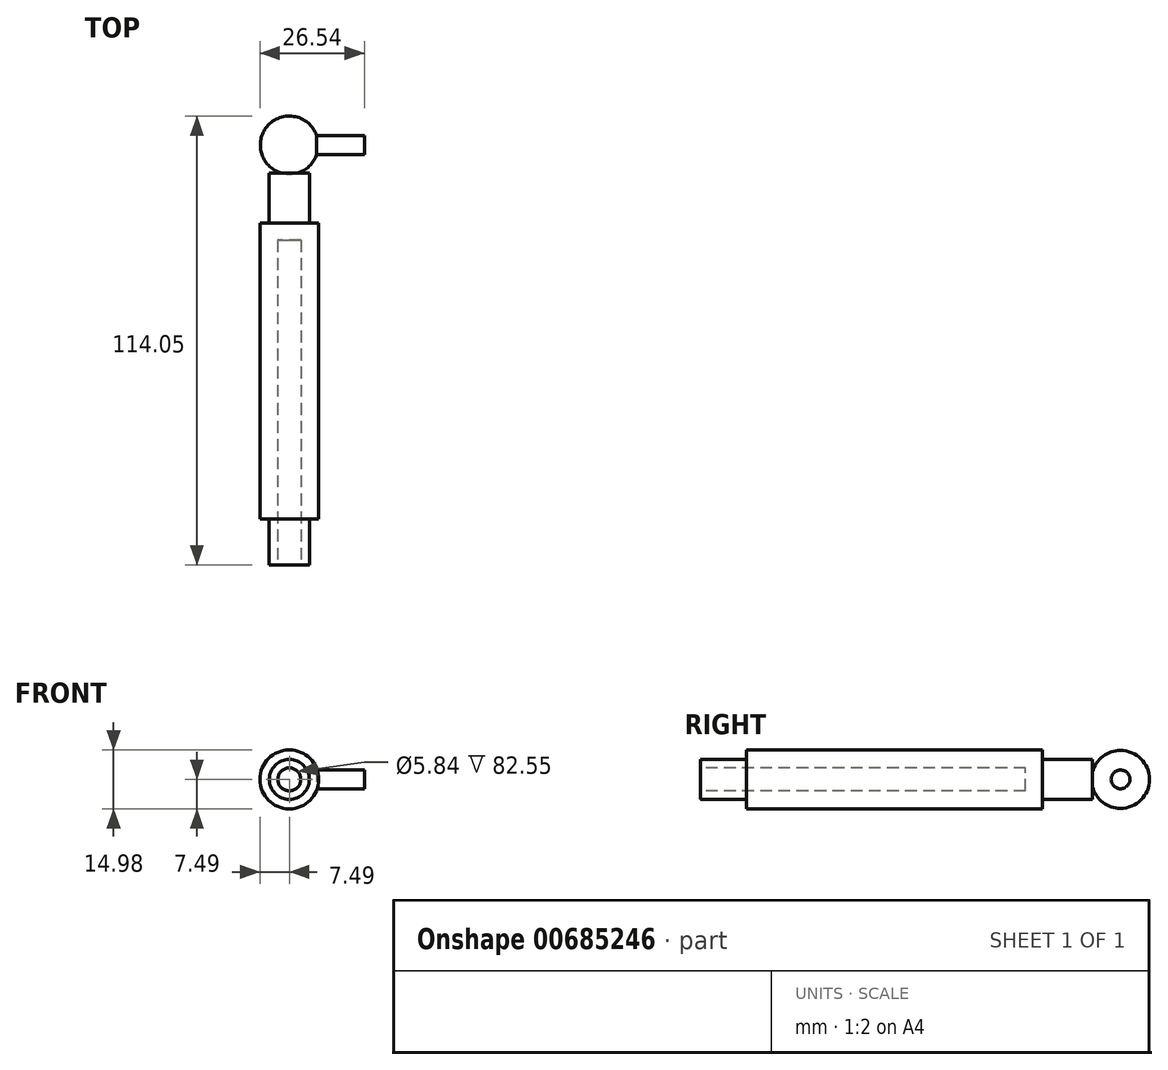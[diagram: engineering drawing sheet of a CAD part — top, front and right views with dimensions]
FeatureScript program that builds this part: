
annotation { "Feature Type Name" : "Feature", "Feature Type Description" : "" }
export const myFeature = defineFeature(function(context is Context, id is Id, definition is map)
    precondition{}
    {
        {
            var Q0;
            Q0=qCreatedBy(makeId("Front.planeOp"),FACE);
            var sketch = newSketch(context, id + "F0", { "sketchPlane" : qUnion([Q0])});
            skCircle(sketch, "E0", {"center": v(0, 0) * mm, "radius": 7.5 * mm});
            skSolve(sketch);
        }
        {
            var Q0;
            Q0 = qSketchRegion(id + "F0", true);
            extrude(context, id + "F1", {"entities" : qUnion([Q0]), "depth" : 75.18 * mm, "offsetDistance" : 25.4 * mm});
        }
        {
            var Q0;
            Q0=makeQuery(id+"F1.opExtrude","CAP_FACE",FACE,{"disambiguationData":[OSD([sQuery(id+"F0.wireOp",EDGE,"E0")])],"isStart":true});
            var sketch = newSketch(context, id + "F2", { "sketchPlane" : qUnion([Q0])});
            skCircle(sketch, "E1", {"center": v(0, 0) * mm, "radius": 5.08 * mm});
            skSolve(sketch);
        }
        {
            var Q0;
            Q0 = qSketchRegion(id + "F2", true);
            extrude(context, id + "F3", {"entities" : qUnion([Q0]), "operationType" : NewBodyOperationType.ADD, "depth" : 12.7 * mm, "offsetDistance" : 25.4 * mm});
        }
        {
            var Q0;
            Q0=makeQuery(id+"F1.opExtrude","CAP_FACE",FACE,{"disambiguationData":[OSD([sQuery(id+"F0.wireOp",EDGE,"E0")])],"isStart":false});
            var sketch = newSketch(context, id + "F4", { "sketchPlane" : qUnion([Q0])});
            skCircle(sketch, "E2", {"center": v(0, 0) * mm, "radius": 5.08 * mm});
            skSolve(sketch);
        }
        {
            var Q0;
            Q0 = qSketchRegion(id + "F4", true);
            extrude(context, id + "F5", {"entities" : qUnion([Q0]), "operationType" : NewBodyOperationType.ADD, "depth" : 11.68 * mm, "offsetDistance" : 25.4 * mm});
        }
        {
            var Q0;
            Q0=qCreatedBy(makeId("Right.planeOp"),FACE);
            var sketch = newSketch(context, id + "F6", { "sketchPlane" : qUnion([Q0])});
            skCircle(sketch, "E3", {"center": v(19.81, 0) * mm, "radius": 7.37 * mm});
            skLineSegment(sketch, "E4", {"start": v(19.81, 0) * mm, "end": v(19.81, 7.37) * mm});
            skLineSegment(sketch, "E5", {"start": v(19.81, 7.37) * mm, "end": v(19.81, -7.37) * mm});
            skSolve(sketch);
        }
        {
            var Q0;
            {var subQ0=sQuery(id+"F6.wireOp",EDGE,"E5");var subQ4=makeQuery(id+"F6.imprint","IMPRINT",VERTEX,{"derivedFrom":subQ0});Q0=makeQuery(id+"F6.imprint","IMPRINT",FACE,{"disambiguationData":[TD([[makeQuery(id+"F6.imprint","IMPRINT",EDGE,{"disambiguationData":[TD([[subQ4,1.0]])],"derivedFrom":subQ0}),-1.0]])]});}
            var Q1;
            Q1=sQuery(id+"F6.wireOp",EDGE,"E4");
            revolve(context, id + "F7", {"entities" : qUnion([Q0]), "axis" : qUnion([Q1]), "revolveType" : RevolveType.FULL});
        }
        {
            var Q0;
            Q0=makeQuery(id+"F5.opExtrude","CAP_FACE",FACE,{"disambiguationData":[OSD([sQuery(id+"F4.wireOp",EDGE,"E2")])],"isStart":false});
            var sketch = newSketch(context, id + "F8", { "sketchPlane" : qUnion([Q0])});
            skCircle(sketch, "E6", {"center": v(0, 0) * mm, "radius": 2.92 * mm});
            skSolve(sketch);
        }
        {
            var Q0;
            Q0 = qSketchRegion(id + "F8", true);
            extrude(context, id + "F9", {"entities" : qUnion([Q0]), "operationType" : NewBodyOperationType.REMOVE, "oppositeDirection" : true, "depth" : 82.55 * mm, "offsetDistance" : 25.4 * mm});
        }
        {
            var Q0;
            Q0=qCreatedBy(makeId("Right.planeOp"),FACE);
            var sketch = newSketch(context, id + "F10", { "sketchPlane" : qUnion([Q0])});
            skCircle(sketch, "E7", {"center": v(19.81, 0) * mm, "radius": 2.38 * mm});
            skSolve(sketch);
        }
        {
            var Q0;
            Q0 = qSketchRegion(id + "F10", true);
            extrude(context, id + "F11", {"entities" : qUnion([Q0]), "operationType" : NewBodyOperationType.ADD, "depth" : 19.05 * mm, "offsetDistance" : 25.4 * mm});
        }
    });
